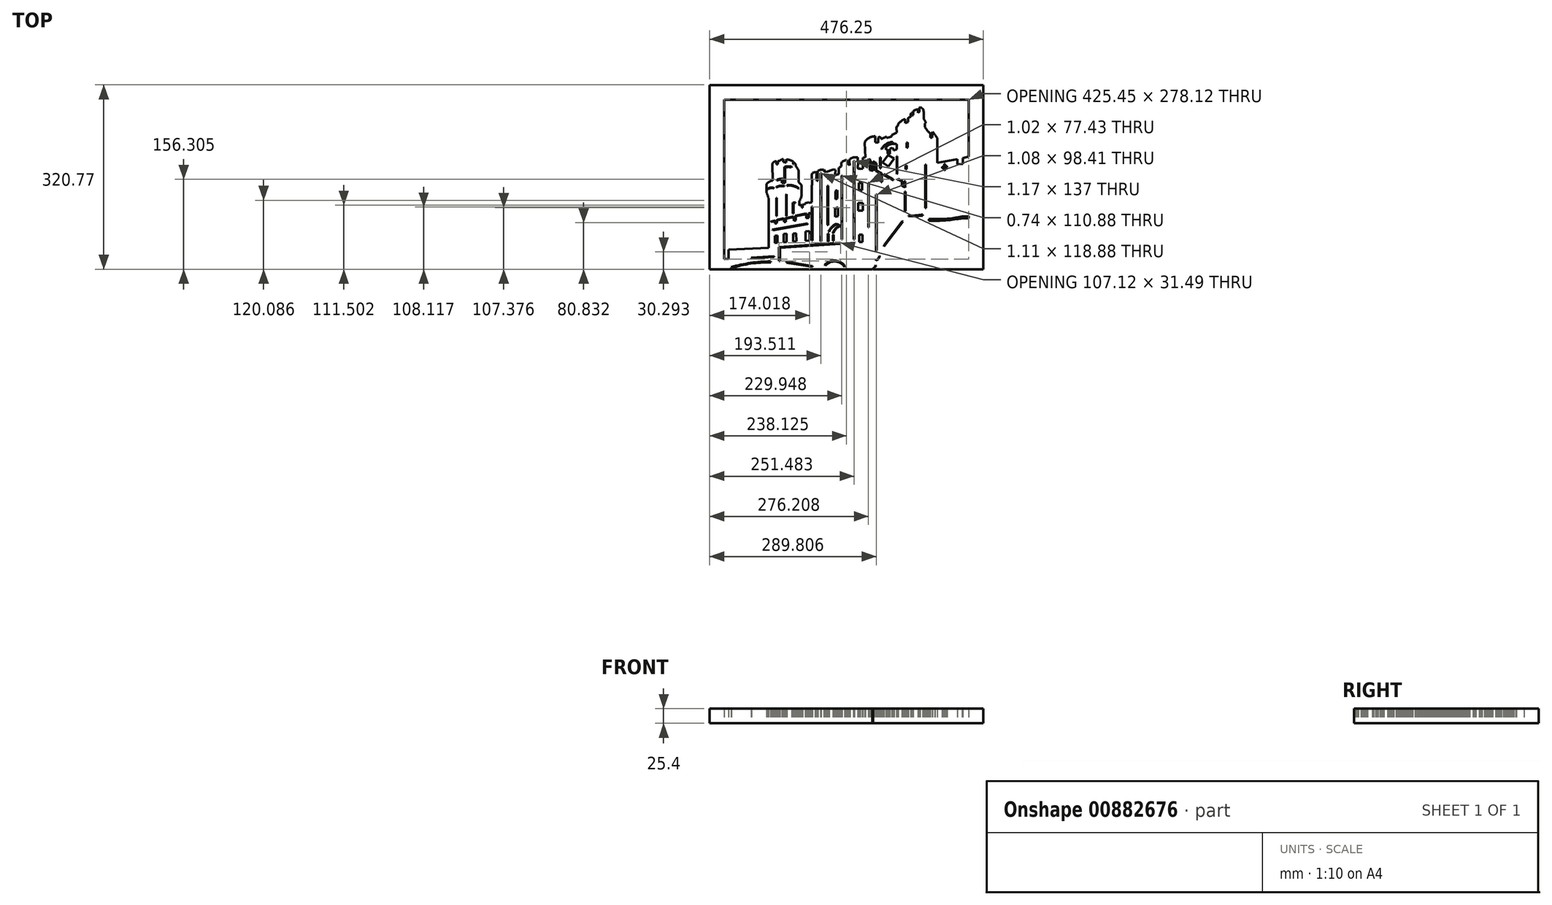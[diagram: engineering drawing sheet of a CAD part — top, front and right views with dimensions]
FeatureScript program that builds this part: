
annotation { "Feature Type Name" : "Feature", "Feature Type Description" : "" }
export const myFeature = defineFeature(function(context is Context, id is Id, definition is map)
    precondition{}
    {
        {
            var Q0;
            Q0=qCreatedBy(makeId("Top.planeOp"),FACE);
            var sketch = newSketch(context, id + "F0", { "sketchPlane" : qUnion([Q0])});
            skLineSegment(sketch, "E0", {"start": v(-417.82, 33.8) * mm, "end": v(-348.2, 37.39) * mm});
            skLineSegment(sketch, "E1", {"start": v(-348.2, 37.39) * mm, "end": v(-348.2, 120.56) * mm});
            skLineSegment(sketch, "E2", {"start": v(-348.2, 120.56) * mm, "end": v(-348.2, 123.62) * mm});
            skLineSegment(sketch, "E3", {"start": v(-348.2, 123.62) * mm, "end": v(-349.5, 125.19) * mm});
            skLineSegment(sketch, "E4", {"start": v(-349.5, 125.19) * mm, "end": v(-349.5, 127.92) * mm});
            skLineSegment(sketch, "E5", {"start": v(-349.5, 127.92) * mm, "end": v(-350.58, 129.49) * mm});
            skLineSegment(sketch, "E6", {"start": v(-350.58, 129.49) * mm, "end": v(-350.58, 131.44) * mm});
            skLineSegment(sketch, "E7", {"start": v(-350.58, 131.44) * mm, "end": v(-351.85, 133) * mm});
            skLineSegment(sketch, "E8", {"start": v(-351.85, 133) * mm, "end": v(-351.85, 148.63) * mm});
            skArc(sketch, "E9", {"start": v(-338.96, 154.6) * mm, "mid": v(-346, 152.92) * mm, "end": v(-351.85, 148.63) * mm});
            skLineSegment(sketch, "E10", {"start": v(-341.3, 154.37) * mm, "end": v(-342.08, 182.63) * mm});
            skLineSegment(sketch, "E11", {"start": v(-334.85, 187.8) * mm, "end": v(-334.85, 182.73) * mm});
            skLineSegment(sketch, "E12", {"start": v(-332.02, 188.4) * mm, "end": v(-332.02, 182.83) * mm});
            skLineSegment(sketch, "E13", {"start": v(-322.54, 191.42) * mm, "end": v(-322.54, 186.15) * mm});
            skLineSegment(sketch, "E14", {"start": v(-317.95, 191.23) * mm, "end": v(-317.95, 185.85) * mm});
            skLineSegment(sketch, "E15", {"start": v(-305.55, 187.32) * mm, "end": v(-305.55, 182.63) * mm});
            skLineSegment(sketch, "E16", {"start": v(-304.86, 186.15) * mm, "end": v(-304.86, 182.63) * mm});
            skLineSegment(sketch, "E17", {"start": v(-301.15, 182.63) * mm, "end": v(-301.15, 179.4) * mm});
            skLineSegment(sketch, "E18", {"start": v(-301.15, 179.4) * mm, "end": v(-298.12, 175.6) * mm});
            skLineSegment(sketch, "E19", {"start": v(-298.12, 175.6) * mm, "end": v(-298.12, 174.42) * mm});
            skLineSegment(sketch, "E20", {"start": v(-298.12, 174.42) * mm, "end": v(-296.26, 172.76) * mm});
            skLineSegment(sketch, "E21", {"start": v(-296.26, 172.76) * mm, "end": v(-296.26, 151.56) * mm});
            skLineSegment(sketch, "E22", {"start": v(-296.26, 151.56) * mm, "end": v(-295, 150.2) * mm});
            skLineSegment(sketch, "E23", {"start": v(-295, 150.2) * mm, "end": v(-294.62, 150.54) * mm});
            skLineSegment(sketch, "E24", {"start": v(-294.62, 150.54) * mm, "end": v(-291.12, 146.77) * mm});
            skLineSegment(sketch, "E25", {"start": v(-291.12, 146.77) * mm, "end": v(-291.12, 126.56) * mm});
            skLineSegment(sketch, "E26", {"start": v(-291.12, 126.56) * mm, "end": v(-291.97, 126.56) * mm});
            skLineSegment(sketch, "E27", {"start": v(-291.97, 126.56) * mm, "end": v(-291.97, 125) * mm});
            skLineSegment(sketch, "E28", {"start": v(-291.97, 125) * mm, "end": v(-291.97, 123.72) * mm});
            skLineSegment(sketch, "E29", {"start": v(-291.97, 123.72) * mm, "end": v(-293.24, 123.72) * mm});
            skLineSegment(sketch, "E30", {"start": v(-293.24, 123.72) * mm, "end": v(-293.72, 119.86) * mm});
            skLineSegment(sketch, "E31", {"start": v(-293.72, 119.86) * mm, "end": v(-294.7, 119.13) * mm});
            skLineSegment(sketch, "E32", {"start": v(-294.7, 119.13) * mm, "end": v(-294.7, 110.83) * mm});
            skLineSegment(sketch, "E33", {"start": v(-294.7, 110.83) * mm, "end": v(-291.77, 111.56) * mm});
            skLineSegment(sketch, "E34", {"start": v(-291.77, 111.56) * mm, "end": v(-290.52, 111.34) * mm});
            skLineSegment(sketch, "E35", {"start": v(-290.52, 111.34) * mm, "end": v(-290.64, 106.87) * mm});
            skLineSegment(sketch, "E36", {"start": v(-290.64, 106.87) * mm, "end": v(-289.3, 107.1) * mm});
            skLineSegment(sketch, "E37", {"start": v(-289.3, 107.1) * mm, "end": v(-289.42, 112.1) * mm});
            skLineSegment(sketch, "E38", {"start": v(-289.42, 112.1) * mm, "end": v(-284.54, 113.5) * mm});
            skLineSegment(sketch, "E39", {"start": v(-284.54, 113.5) * mm, "end": v(-284.6, 114.66) * mm});
            skLineSegment(sketch, "E40", {"start": v(-284.6, 114.66) * mm, "end": v(-278.44, 116.4) * mm});
            skLineSegment(sketch, "E41", {"start": v(-278.44, 116.4) * mm, "end": v(-278.44, 115.41) * mm});
            skLineSegment(sketch, "E42", {"start": v(-278.44, 115.41) * mm, "end": v(-273.18, 116.66) * mm});
            skLineSegment(sketch, "E43", {"start": v(-273.18, 116.66) * mm, "end": v(-273.18, 145.82) * mm});
            skLineSegment(sketch, "E44", {"start": v(-273.18, 145.82) * mm, "end": v(-272.9, 146.87) * mm});
            skLineSegment(sketch, "E45", {"start": v(-272.9, 146.87) * mm, "end": v(-273.18, 165.14) * mm});
            skLineSegment(sketch, "E46", {"start": v(-273.18, 165.14) * mm, "end": v(-271.8, 167.56) * mm});
            skLineSegment(sketch, "E47", {"start": v(-271.8, 167.56) * mm, "end": v(-267.44, 169.08) * mm});
            skLineSegment(sketch, "E48", {"start": v(-267.44, 169.08) * mm, "end": v(-265.5, 168.53) * mm});
            skLineSegment(sketch, "E49", {"start": v(-265.5, 168.53) * mm, "end": v(-264.81, 166.87) * mm});
            skLineSegment(sketch, "E50", {"start": v(-264.81, 166.87) * mm, "end": v(-264.81, 161.9) * mm});
            skLineSegment(sketch, "E51", {"start": v(-264.81, 161.9) * mm, "end": v(-265.23, 160.93) * mm});
            skLineSegment(sketch, "E52", {"start": v(-265.23, 160.93) * mm, "end": v(-265.37, 158.65) * mm});
            skLineSegment(sketch, "E53", {"start": v(-265.37, 158.65) * mm, "end": v(-264.74, 158.3) * mm});
            skLineSegment(sketch, "E54", {"start": v(-264.74, 158.3) * mm, "end": v(-264.6, 153.2) * mm});
            skLineSegment(sketch, "E55", {"start": v(-264.6, 153.2) * mm, "end": v(-262.88, 153.95) * mm});
            skLineSegment(sketch, "E56", {"start": v(-262.88, 153.95) * mm, "end": v(-263.22, 168.46) * mm});
            skLineSegment(sketch, "E57", {"start": v(-263.22, 168.46) * mm, "end": v(-262.46, 171.15) * mm});
            skLineSegment(sketch, "E58", {"start": v(-262.46, 171.15) * mm, "end": v(-257.77, 173.09) * mm});
            skLineSegment(sketch, "E59", {"start": v(-257.77, 173.09) * mm, "end": v(-252.52, 172.95) * mm});
            skLineSegment(sketch, "E60", {"start": v(-252.52, 172.95) * mm, "end": v(-250.72, 170.25) * mm});
            skLineSegment(sketch, "E61", {"start": v(-250.72, 170.25) * mm, "end": v(-250.93, 169.9) * mm});
            skLineSegment(sketch, "E62", {"start": v(-250.93, 169.9) * mm, "end": v(-251.2, 169.29) * mm});
            skLineSegment(sketch, "E63", {"start": v(-251.2, 169.29) * mm, "end": v(-249.75, 169.84) * mm});
            skLineSegment(sketch, "E64", {"start": v(-249.75, 169.84) * mm, "end": v(-247.82, 169.29) * mm});
            skLineSegment(sketch, "E65", {"start": v(-247.82, 169.29) * mm, "end": v(-235.04, 173.91) * mm});
            skLineSegment(sketch, "E66", {"start": v(-235.04, 173.91) * mm, "end": v(-232.9, 173.22) * mm});
            skLineSegment(sketch, "E67", {"start": v(-232.9, 173.22) * mm, "end": v(-232.2, 171.63) * mm});
            skLineSegment(sketch, "E68", {"start": v(-232.2, 171.63) * mm, "end": v(-232.48, 164.86) * mm});
            skLineSegment(sketch, "E69", {"start": v(-232.48, 164.86) * mm, "end": v(-233.06, 164.41) * mm});
            skLineSegment(sketch, "E70", {"start": v(-233.06, 164.41) * mm, "end": v(-233.06, 163.4) * mm});
            skLineSegment(sketch, "E71", {"start": v(-233.06, 163.4) * mm, "end": v(-226.35, 165.63) * mm});
            skLineSegment(sketch, "E72", {"start": v(-226.35, 165.63) * mm, "end": v(-226.35, 174.75) * mm});
            skLineSegment(sketch, "E73", {"start": v(-226.35, 174.75) * mm, "end": v(-225.83, 176.73) * mm});
            skLineSegment(sketch, "E74", {"start": v(-225.83, 176.73) * mm, "end": v(-221.94, 178.7) * mm});
            skLineSegment(sketch, "E75", {"start": v(-221.94, 178.7) * mm, "end": v(-221.94, 184.4) * mm});
            skLineSegment(sketch, "E76", {"start": v(-221.94, 184.4) * mm, "end": v(-220.25, 187.41) * mm});
            skLineSegment(sketch, "E77", {"start": v(-220.25, 187.41) * mm, "end": v(-213.63, 189.97) * mm});
            skLineSegment(sketch, "E78", {"start": v(-213.63, 189.97) * mm, "end": v(-211.6, 189.1) * mm});
            skLineSegment(sketch, "E79", {"start": v(-211.6, 189.1) * mm, "end": v(-210.75, 187.43) * mm});
            skLineSegment(sketch, "E80", {"start": v(-210.75, 187.43) * mm, "end": v(-210.75, 183.11) * mm});
            skLineSegment(sketch, "E81", {"start": v(-210.75, 183.11) * mm, "end": v(-209.16, 182.36) * mm});
            skLineSegment(sketch, "E82", {"start": v(-209.16, 182.36) * mm, "end": v(-207.47, 180.5) * mm});
            skLineSegment(sketch, "E83", {"start": v(-207.47, 180.5) * mm, "end": v(-207.7, 189.68) * mm});
            skLineSegment(sketch, "E84", {"start": v(-207.7, 189.68) * mm, "end": v(-206.6, 192.23) * mm});
            skLineSegment(sketch, "E85", {"start": v(-206.6, 192.23) * mm, "end": v(-200.85, 194.73) * mm});
            skLineSegment(sketch, "E86", {"start": v(-200.85, 194.73) * mm, "end": v(-193.01, 194.85) * mm});
            skLineSegment(sketch, "E87", {"start": v(-193.01, 194.85) * mm, "end": v(-192.78, 181.55) * mm});
            skLineSegment(sketch, "E88", {"start": v(-192.78, 181.55) * mm, "end": v(-193.53, 180.68) * mm});
            skLineSegment(sketch, "E89", {"start": v(-193.53, 180.68) * mm, "end": v(-193.42, 175.74) * mm});
            skLineSegment(sketch, "E90", {"start": v(-193.42, 175.74) * mm, "end": v(-192.55, 175.04) * mm});
            skLineSegment(sketch, "E91", {"start": v(-192.55, 175.04) * mm, "end": v(-189, 175.1) * mm});
            skLineSegment(sketch, "E92", {"start": v(-189, 175.1) * mm, "end": v(-189.06, 174.52) * mm});
            skLineSegment(sketch, "E93", {"start": v(-189.06, 174.52) * mm, "end": v(-184.3, 174.75) * mm});
            skLineSegment(sketch, "E94", {"start": v(-184.3, 174.75) * mm, "end": v(-184.65, 194.33) * mm});
            skLineSegment(sketch, "E95", {"start": v(-184.65, 194.33) * mm, "end": v(-180.17, 194.44) * mm});
            skLineSegment(sketch, "E96", {"start": v(-180.17, 194.44) * mm, "end": v(-180.99, 220.35) * mm});
            skLineSegment(sketch, "E97", {"start": v(-180.99, 220.35) * mm, "end": v(-180.35, 220.99) * mm});
            skLineSegment(sketch, "E98", {"start": v(-180.35, 220.99) * mm, "end": v(-180.35, 222.67) * mm});
            skLineSegment(sketch, "E99", {"start": v(-162.98, 231.27) * mm, "end": v(-162.69, 220.47) * mm});
            skLineSegment(sketch, "E100", {"start": v(-162.69, 220.47) * mm, "end": v(-157.4, 220.35) * mm});
            skLineSegment(sketch, "E101", {"start": v(-157.4, 220.35) * mm, "end": v(-157.8, 228.66) * mm});
            skLineSegment(sketch, "E102", {"start": v(-157.8, 228.66) * mm, "end": v(-156.59, 230.51) * mm});
            skLineSegment(sketch, "E103", {"start": v(-152.76, 228.37) * mm, "end": v(-152.81, 226.74) * mm});
            skLineSegment(sketch, "E104", {"start": v(-152.81, 226.74) * mm, "end": v(-143.17, 230.75) * mm});
            skLineSegment(sketch, "E105", {"start": v(-143.17, 230.75) * mm, "end": v(-143, 228.2) * mm});
            skLineSegment(sketch, "E106", {"start": v(-143, 228.2) * mm, "end": v(-134.4, 231.15) * mm});
            skLineSegment(sketch, "E107", {"start": v(-134.4, 231.15) * mm, "end": v(-134.4, 233.42) * mm});
            skLineSegment(sketch, "E108", {"start": v(-134.4, 233.42) * mm, "end": v(-125.63, 237.72) * mm});
            skLineSegment(sketch, "E109", {"start": v(-125.63, 237.72) * mm, "end": v(-126.2, 246.37) * mm});
            skLineSegment(sketch, "E110", {"start": v(-126.2, 246.37) * mm, "end": v(-124.52, 249.63) * mm});
            skLineSegment(sketch, "E111", {"start": v(-124.52, 249.63) * mm, "end": v(-123.36, 249.63) * mm});
            skLineSegment(sketch, "E112", {"start": v(-123.36, 249.63) * mm, "end": v(-123.36, 252) * mm});
            skLineSegment(sketch, "E113", {"start": v(-110.99, 261.3) * mm, "end": v(-110.99, 259.68) * mm});
            skLineSegment(sketch, "E114", {"start": v(-110.99, 259.68) * mm, "end": v(-110.58, 259.68) * mm});
            skLineSegment(sketch, "E115", {"start": v(-110.58, 259.68) * mm, "end": v(-110.58, 254.16) * mm});
            skLineSegment(sketch, "E116", {"start": v(-110.58, 254.16) * mm, "end": v(-105.53, 256.07) * mm});
            skLineSegment(sketch, "E117", {"start": v(-105.53, 256.07) * mm, "end": v(-105.53, 263.4) * mm});
            skLineSegment(sketch, "E118", {"start": v(-101.23, 269.96) * mm, "end": v(-101.23, 267.34) * mm});
            skLineSegment(sketch, "E119", {"start": v(-101.23, 267.34) * mm, "end": v(-100.3, 266.12) * mm});
            skLineSegment(sketch, "E120", {"start": v(-100.3, 266.12) * mm, "end": v(-100.3, 265.43) * mm});
            skLineSegment(sketch, "E121", {"start": v(-101.23, 269.96) * mm, "end": v(-99.84, 271.93) * mm});
            skLineSegment(sketch, "E122", {"start": v(-99.84, 271.93) * mm, "end": v(-98.9, 271.93) * mm});
            skLineSegment(sketch, "E123", {"start": v(-98.9, 271.93) * mm, "end": v(-98.15, 270.94) * mm});
            skLineSegment(sketch, "E124", {"start": v(-98.15, 270.94) * mm, "end": v(-98.58, 270.4) * mm});
            skLineSegment(sketch, "E125", {"start": v(-98.58, 270.4) * mm, "end": v(-98.58, 268.34) * mm});
            skLineSegment(sketch, "E126", {"start": v(-98.58, 268.34) * mm, "end": v(-97.95, 267.75) * mm});
            skLineSegment(sketch, "E127", {"start": v(-97.95, 267.75) * mm, "end": v(-96.44, 268.5) * mm});
            skLineSegment(sketch, "E128", {"start": v(-96.44, 268.5) * mm, "end": v(-96.44, 274.96) * mm});
            skLineSegment(sketch, "E129", {"start": v(-88.42, 277.86) * mm, "end": v(-88.42, 272.05) * mm});
            skLineSegment(sketch, "E130", {"start": v(-88.42, 272.05) * mm, "end": v(-86.15, 274.09) * mm});
            skLineSegment(sketch, "E131", {"start": v(-86.15, 274.09) * mm, "end": v(-86.15, 281.17) * mm});
            skLineSegment(sketch, "E132", {"start": v(-86.15, 281.17) * mm, "end": v(-84.83, 282.36) * mm});
            skLineSegment(sketch, "E133", {"start": v(-78.9, 277.8) * mm, "end": v(-78.9, 276.87) * mm});
            skLineSegment(sketch, "E134", {"start": v(-78.9, 276.87) * mm, "end": v(-79.24, 276.61) * mm});
            skLineSegment(sketch, "E135", {"start": v(-79.24, 276.61) * mm, "end": v(-79.24, 274.96) * mm});
            skLineSegment(sketch, "E136", {"start": v(-79.24, 274.96) * mm, "end": v(-78.28, 274.46) * mm});
            skLineSegment(sketch, "E137", {"start": v(-78.28, 274.46) * mm, "end": v(-78.28, 261.63) * mm});
            skLineSegment(sketch, "E138", {"start": v(-75.28, 255.92) * mm, "end": v(-75.28, 254.54) * mm});
            skLineSegment(sketch, "E139", {"start": v(-75.28, 254.54) * mm, "end": v(-76.1, 253.85) * mm});
            skLineSegment(sketch, "E140", {"start": v(-76.1, 253.85) * mm, "end": v(-76.18, 247.29) * mm});
            skLineSegment(sketch, "E141", {"start": v(-76.18, 247.29) * mm, "end": v(-71.83, 241.14) * mm});
            skLineSegment(sketch, "E142", {"start": v(-71.83, 241.14) * mm, "end": v(-71.69, 239.7) * mm});
            skLineSegment(sketch, "E143", {"start": v(-71.69, 239.7) * mm, "end": v(-70.88, 239.77) * mm});
            skLineSegment(sketch, "E144", {"start": v(-70.88, 239.77) * mm, "end": v(-67.2, 235.96) * mm});
            skLineSegment(sketch, "E145", {"start": v(-67.2, 235.96) * mm, "end": v(-67.2, 229.12) * mm});
            skLineSegment(sketch, "E146", {"start": v(-67.2, 229.12) * mm, "end": v(-64.02, 229.12) * mm});
            skLineSegment(sketch, "E147", {"start": v(-64.02, 229.12) * mm, "end": v(-64.02, 237.48) * mm});
            skLineSegment(sketch, "E148", {"start": v(-64.02, 237.48) * mm, "end": v(-63.26, 239.14) * mm});
            skLineSegment(sketch, "E149", {"start": v(-63.26, 239.14) * mm, "end": v(-59.18, 234.5) * mm});
            skLineSegment(sketch, "E150", {"start": v(-59.18, 234.5) * mm, "end": v(-59.18, 233.4) * mm});
            skLineSegment(sketch, "E151", {"start": v(-59.18, 233.4) * mm, "end": v(-58.45, 233.22) * mm});
            skLineSegment(sketch, "E152", {"start": v(-58.45, 233.22) * mm, "end": v(-55, 228.36) * mm});
            skLineSegment(sketch, "E153", {"start": v(-55, 228.36) * mm, "end": v(-55, 185.15) * mm});
            skLineSegment(sketch, "E154", {"start": v(-55, 185.15) * mm, "end": v(-20.1, 191.5) * mm});
            skLineSegment(sketch, "E155", {"start": v(-20.1, 191.5) * mm, "end": v(-20.1, 182.51) * mm});
            skLineSegment(sketch, "E156", {"start": v(-20.1, 182.51) * mm, "end": v(-10.63, 183.4) * mm});
            skLineSegment(sketch, "E157", {"start": v(-10.63, 183.4) * mm, "end": v(-10.63, 193.16) * mm});
            skLineSegment(sketch, "E158", {"start": v(-10.63, 193.16) * mm, "end": v(0, 195.7) * mm});
            skArc(sketch, "E159", {"start": v(-334.85, 187.8) * mm, "mid": v(-339.36, 186.46) * mm, "end": v(-342.08, 182.63) * mm});
            skArc(sketch, "E160", {"start": v(-322.54, 191.42) * mm, "mid": v(-326.28, 190.63) * mm, "end": v(-329.38, 188.4) * mm});
            skArc(sketch, "E161", {"start": v(-305.55, 187.32) * mm, "mid": v(-311.5, 190.08) * mm, "end": v(-317.95, 191.23) * mm});
            skLineSegment(sketch, "E162", {"start": v(-304.86, 186.15) * mm, "end": v(-301.15, 182.63) * mm});
            skLineSegment(sketch, "E163", {"start": v(-329.38, 188.4) * mm, "end": v(-332.02, 188.4) * mm});
            skLineSegment(sketch, "E164", {"start": v(-332.02, 182.83) * mm, "end": v(-334.85, 182.73) * mm});
            skArc(sketch, "E165", {"start": v(-317.95, 185.85) * mm, "mid": v(-320.23, 186.22) * mm, "end": v(-322.54, 186.15) * mm});
            skLineSegment(sketch, "E166", {"start": v(-304.86, 182.63) * mm, "end": v(-305.55, 182.63) * mm});
            skArc(sketch, "E167", {"start": v(-162.98, 231.27) * mm, "mid": v(-172.68, 229.03) * mm, "end": v(-180.35, 222.67) * mm});
            skArc(sketch, "E168", {"start": v(-152.76, 228.37) * mm, "mid": v(-154.48, 229.79) * mm, "end": v(-156.59, 230.51) * mm});
            skArc(sketch, "E169", {"start": v(-110.99, 261.3) * mm, "mid": v(-117.84, 257.54) * mm, "end": v(-123.36, 252) * mm});
            skArc(sketch, "E170", {"start": v(-100.3, 265.43) * mm, "mid": v(-103.02, 264.69) * mm, "end": v(-105.53, 263.4) * mm});
            skArc(sketch, "E171", {"start": v(-88.42, 277.86) * mm, "mid": v(-92.77, 277.35) * mm, "end": v(-96.44, 274.96) * mm});
            skArc(sketch, "E172", {"start": v(-78.9, 277.8) * mm, "mid": v(-81.66, 280.35) * mm, "end": v(-84.83, 282.36) * mm});
            skArc(sketch, "E173", {"start": v(-75.28, 255.92) * mm, "mid": v(-76.56, 258.9) * mm, "end": v(-78.28, 261.63) * mm});
            skLineSegment(sketch, "E174.bottom", {"start": v(0, 0) * mm, "end": v(-425.45, 0) * mm});
            skLineSegment(sketch, "E174.top", {"start": v(0, 295.37) * mm, "end": v(-425.45, 295.37) * mm});
            skLineSegment(sketch, "E174.left", {"start": v(0, 0) * mm, "end": v(0, 295.37) * mm});
            skLineSegment(sketch, "E174.right", {"start": v(-425.45, 17.24) * mm, "end": v(-425.45, 295.37) * mm});
            skLineSegment(sketch, "E175", {"start": v(-417.82, 33.8) * mm, "end": v(-417.82, 18.22) * mm});
            skLineSegment(sketch, "E176", {"start": v(-417.82, 18.22) * mm, "end": v(-425.45, 17.24) * mm});
            skLineSegment(sketch, "E177", {"start": v(-115.55, 83.88) * mm, "end": v(-147.82, 41.94) * mm});
            skLineSegment(sketch, "E178", {"start": v(-147.82, 41.94) * mm, "end": v(-147.82, 39.84) * mm});
            skLineSegment(sketch, "E179", {"start": v(-147.82, 39.84) * mm, "end": v(-114.82, 82.86) * mm});
            skLineSegment(sketch, "E180", {"start": v(-114.82, 82.86) * mm, "end": v(-115.55, 83.88) * mm});
            skArc(sketch, "E181", {"start": v(-69.74, 87.47) * mm, "mid": v(-40.42, 87.66) * mm, "end": v(-11.37, 91.58) * mm});
            skArc(sketch, "E182", {"start": v(-69.74, 84.45) * mm, "mid": v(-40.17, 85.13) * mm, "end": v(-10.82, 88.84) * mm});
            skLineSegment(sketch, "E183", {"start": v(-69.74, 84.45) * mm, "end": v(-69.74, 87.47) * mm});
            skLineSegment(sketch, "E184", {"start": v(-10.82, 88.84) * mm, "end": v(-11.37, 91.58) * mm});
            skLineSegment(sketch, "E185", {"start": v(-108.23, 174.38) * mm, "end": v(-108.23, 180.96) * mm});
            skLineSegment(sketch, "E186", {"start": v(-108.23, 180.96) * mm, "end": v(-110.07, 180.29) * mm});
            skLineSegment(sketch, "E187", {"start": v(-110.07, 180.29) * mm, "end": v(-110.07, 173.7) * mm});
            skLineSegment(sketch, "E188", {"start": v(-110.07, 173.7) * mm, "end": v(-108.23, 174.38) * mm});
            skLineSegment(sketch, "E189", {"start": v(-106.18, 220.87) * mm, "end": v(-108.12, 220.2) * mm});
            skLineSegment(sketch, "E190", {"start": v(-108.12, 220.2) * mm, "end": v(-108.02, 210.99) * mm});
            skLineSegment(sketch, "E191", {"start": v(-108.02, 210.99) * mm, "end": v(-106.18, 211.86) * mm});
            skLineSegment(sketch, "E192", {"start": v(-106.18, 211.86) * mm, "end": v(-106.18, 220.87) * mm});
            skLineSegment(sketch, "E193", {"start": v(-144.26, 211.67) * mm, "end": v(-144.26, 208.08) * mm});
            skLineSegment(sketch, "E194", {"start": v(-144.26, 208.08) * mm, "end": v(-140.97, 208.86) * mm});
            skLineSegment(sketch, "E195", {"start": v(-140.97, 208.86) * mm, "end": v(-140.97, 201.1) * mm});
            skLineSegment(sketch, "E196", {"start": v(-140.97, 201.1) * mm, "end": v(-139.7, 201.1) * mm});
            skLineSegment(sketch, "E197", {"start": v(-139.7, 201.1) * mm, "end": v(-139.7, 200.28) * mm});
            skLineSegment(sketch, "E198", {"start": v(-139.7, 200.28) * mm, "end": v(-137.1, 200.62) * mm});
            skLineSegment(sketch, "E199", {"start": v(-137.1, 200.62) * mm, "end": v(-137.1, 209.6) * mm});
            skLineSegment(sketch, "E200", {"start": v(-137.1, 209.6) * mm, "end": v(-133.78, 211.51) * mm});
            skLineSegment(sketch, "E201", {"start": v(-133.78, 211.51) * mm, "end": v(-130.79, 209.1) * mm});
            skLineSegment(sketch, "E202", {"start": v(-130.79, 209.1) * mm, "end": v(-130.79, 206.84) * mm});
            skLineSegment(sketch, "E203", {"start": v(-130.79, 206.84) * mm, "end": v(-125.34, 208.8) * mm});
            skLineSegment(sketch, "E204", {"start": v(-125.34, 208.8) * mm, "end": v(-125.34, 217.39) * mm});
            skArc(sketch, "E205", {"start": v(-125.34, 217.39) * mm, "mid": v(-135.76, 217.7) * mm, "end": v(-144.26, 211.67) * mm});
            skLineSegment(sketch, "E206", {"start": v(-42.6, 183.06) * mm, "end": v(-42.6, 178.05) * mm});
            skArc(sketch, "E207", {"start": v(-45.61, 178.23) * mm, "mid": v(-46.35, 177) * mm, "end": v(-45.44, 175.9) * mm});
            skArc(sketch, "E208", {"start": v(-38.3, 177.28) * mm, "mid": v(-37.9, 178.49) * mm, "end": v(-38.73, 179.44) * mm});
            skArc(sketch, "E209", {"start": v(-43.14, 174.09) * mm, "mid": v(-41.82, 172.7) * mm, "end": v(-40.48, 174.06) * mm});
            skArc(sketch, "E210", {"start": v(-43.14, 174.09) * mm, "mid": v(-42.7, 174.67) * mm, "end": v(-42.46, 175.37) * mm});
            skArc(sketch, "E211", {"start": v(-41.25, 175.32) * mm, "mid": v(-40.92, 174.66) * mm, "end": v(-40.48, 174.06) * mm});
            skArc(sketch, "E212", {"start": v(-38.73, 179.44) * mm, "mid": v(-39.25, 179.03) * mm, "end": v(-39.75, 178.62) * mm});
            skArc(sketch, "E213", {"start": v(-44.55, 177.6) * mm, "mid": v(-45.04, 177.98) * mm, "end": v(-45.61, 178.23) * mm});
            skArc(sketch, "E214", {"start": v(-45.44, 175.9) * mm, "mid": v(-44.93, 176.13) * mm, "end": v(-44.6, 176.58) * mm});
            skLineSegment(sketch, "E215", {"start": v(-42.6, 183.06) * mm, "end": v(-41.67, 183.06) * mm});
            skLineSegment(sketch, "E216", {"start": v(-41.67, 183.06) * mm, "end": v(-41.67, 178.47) * mm});
            skLineSegment(sketch, "E217", {"start": v(-41.67, 178.47) * mm, "end": v(-39.75, 178.62) * mm});
            skLineSegment(sketch, "E218", {"start": v(-38.3, 177.28) * mm, "end": v(-40.99, 177.28) * mm});
            skLineSegment(sketch, "E219", {"start": v(-40.99, 177.28) * mm, "end": v(-41.52, 176.78) * mm});
            skLineSegment(sketch, "E220", {"start": v(-41.52, 176.78) * mm, "end": v(-41.19, 175.17) * mm});
            skLineSegment(sketch, "E221", {"start": v(-42.46, 175.37) * mm, "end": v(-42.46, 176.85) * mm});
            skLineSegment(sketch, "E222", {"start": v(-42.46, 176.85) * mm, "end": v(-44.35, 176.85) * mm});
            skLineSegment(sketch, "E223", {"start": v(-44.35, 176.85) * mm, "end": v(-44.6, 176.58) * mm});
            skLineSegment(sketch, "E224", {"start": v(-44.55, 177.6) * mm, "end": v(-43.58, 177.6) * mm});
            skLineSegment(sketch, "E225", {"start": v(-43.58, 177.6) * mm, "end": v(-43.29, 178.05) * mm});
            skLineSegment(sketch, "E226", {"start": v(-43.29, 178.05) * mm, "end": v(-42.6, 178.05) * mm});
            skArc(sketch, "E227", {"start": v(-105.02, 92.23) * mm, "mid": v(-92.7, 92.4) * mm, "end": v(-80.4, 93.39) * mm});
            skArc(sketch, "E228", {"start": v(-105.02, 93.31) * mm, "mid": v(-92.66, 93.49) * mm, "end": v(-80.4, 95.06) * mm});
            skLineSegment(sketch, "E229", {"start": v(-105.02, 93.31) * mm, "end": v(-105.02, 92.23) * mm});
            skLineSegment(sketch, "E230", {"start": v(-80.4, 95.06) * mm, "end": v(-80.4, 93.39) * mm});
            skLineSegment(sketch, "E231", {"start": v(-223.27, 44.53) * mm, "end": v(-328.37, 37.04) * mm});
            skLineSegment(sketch, "E232", {"start": v(-328.37, 37.04) * mm, "end": v(-328.37, 14.55) * mm});
            skLineSegment(sketch, "E233", {"start": v(-328.37, 14.55) * mm, "end": v(-330.4, 14.55) * mm});
            skLineSegment(sketch, "E234", {"start": v(-330.4, 14.55) * mm, "end": v(-330.4, 38.29) * mm});
            skLineSegment(sketch, "E235", {"start": v(-330.4, 38.29) * mm, "end": v(-223.52, 46.04) * mm});
            skLineSegment(sketch, "E236", {"start": v(-223.52, 46.04) * mm, "end": v(-223.27, 44.53) * mm});
            skLineSegment(sketch, "E237", {"start": v(-245.1, 48.1) * mm, "end": v(-245.1, 62.05) * mm});
            skLineSegment(sketch, "E238", {"start": v(-236.2, 49.45) * mm, "end": v(-236.2, 59.53) * mm});
            skLineSegment(sketch, "E239", {"start": v(-221.27, 51.97) * mm, "end": v(-221.27, 162.81) * mm});
            skLineSegment(sketch, "E240", {"start": v(-257.9, 48.68) * mm, "end": v(-257.9, 167.27) * mm});
            skLineSegment(sketch, "E241", {"start": v(-273, 108.75) * mm, "end": v(-273, 50.03) * mm});
            skLineSegment(sketch, "E242", {"start": v(-199.95, 51.58) * mm, "end": v(-199.95, 188.59) * mm});
            skLineSegment(sketch, "E243", {"start": v(-175.15, 150.22) * mm, "end": v(-175.15, 73.1) * mm});
            skLineSegment(sketch, "E244", {"start": v(-161.59, 129.68) * mm, "end": v(-161.59, 31.63) * mm});
            skLineSegment(sketch, "E245", {"start": v(-111.2, 101) * mm, "end": v(-111.2, 134.9) * mm});
            skLineSegment(sketch, "E246", {"start": v(-75.55, 182) * mm, "end": v(-75.55, 106.23) * mm});
            skLineSegment(sketch, "E247", {"start": v(-125.52, 196.51) * mm, "end": v(-125.52, 165.55) * mm});
            skLineSegment(sketch, "E248", {"start": v(-154.3, 194.46) * mm, "end": v(-154.3, 175.55) * mm});
            skLineSegment(sketch, "E249", {"start": v(-245.69, 145.4) * mm, "end": v(-245.69, 77.03) * mm});
            skLineSegment(sketch, "E250", {"start": v(-273, 108.75) * mm, "end": v(-272.1, 108.75) * mm});
            skLineSegment(sketch, "E251", {"start": v(-272.1, 108.75) * mm, "end": v(-272.1, 50.18) * mm});
            skLineSegment(sketch, "E252", {"start": v(-272.1, 50.18) * mm, "end": v(-273, 50.03) * mm});
            skLineSegment(sketch, "E253", {"start": v(-257.9, 48.68) * mm, "end": v(-256.78, 48.68) * mm});
            skLineSegment(sketch, "E254", {"start": v(-256.78, 48.68) * mm, "end": v(-256.78, 167.56) * mm});
            skLineSegment(sketch, "E255", {"start": v(-256.78, 167.56) * mm, "end": v(-257.9, 167.27) * mm});
            skLineSegment(sketch, "E256", {"start": v(-245.69, 145.4) * mm, "end": v(-244.96, 145.4) * mm});
            skLineSegment(sketch, "E257", {"start": v(-244.96, 145.4) * mm, "end": v(-244.96, 76.93) * mm});
            skLineSegment(sketch, "E258", {"start": v(-244.96, 76.93) * mm, "end": v(-245.69, 77.03) * mm});
            skLineSegment(sketch, "E259", {"start": v(-221.27, 162.81) * mm, "end": v(-220.53, 162.81) * mm});
            skLineSegment(sketch, "E260", {"start": v(-220.53, 162.81) * mm, "end": v(-220.53, 51.94) * mm});
            skLineSegment(sketch, "E261", {"start": v(-220.53, 51.94) * mm, "end": v(-221.27, 51.97) * mm});
            skLineSegment(sketch, "E262", {"start": v(-199.95, 51.58) * mm, "end": v(-198.78, 51.58) * mm});
            skLineSegment(sketch, "E263", {"start": v(-198.78, 51.58) * mm, "end": v(-198.78, 188.59) * mm});
            skLineSegment(sketch, "E264", {"start": v(-198.78, 188.59) * mm, "end": v(-199.95, 188.59) * mm});
            skLineSegment(sketch, "E265", {"start": v(-175.15, 150.22) * mm, "end": v(-174.13, 150.22) * mm});
            skLineSegment(sketch, "E266", {"start": v(-174.13, 150.22) * mm, "end": v(-174.13, 72.79) * mm});
            skLineSegment(sketch, "E267", {"start": v(-174.13, 72.79) * mm, "end": v(-175.15, 73.1) * mm});
            skLineSegment(sketch, "E268", {"start": v(-161.59, 129.68) * mm, "end": v(-160.5, 130.04) * mm});
            skLineSegment(sketch, "E269", {"start": v(-160.5, 130.04) * mm, "end": v(-160.5, 32.64) * mm});
            skLineSegment(sketch, "E270", {"start": v(-160.5, 32.64) * mm, "end": v(-161.59, 31.63) * mm});
            skLineSegment(sketch, "E271", {"start": v(-111.2, 101) * mm, "end": v(-109.86, 101.44) * mm});
            skLineSegment(sketch, "E272", {"start": v(-109.86, 101.44) * mm, "end": v(-109.86, 134.9) * mm});
            skLineSegment(sketch, "E273", {"start": v(-109.86, 134.9) * mm, "end": v(-111.2, 134.9) * mm});
            skLineSegment(sketch, "E274", {"start": v(-75.55, 106.23) * mm, "end": v(-74.3, 106.27) * mm});
            skLineSegment(sketch, "E275", {"start": v(-74.3, 106.27) * mm, "end": v(-74.3, 182.18) * mm});
            skLineSegment(sketch, "E276", {"start": v(-74.3, 182.18) * mm, "end": v(-75.55, 182) * mm});
            skLineSegment(sketch, "E277", {"start": v(-125.52, 196.51) * mm, "end": v(-124.65, 196.8) * mm});
            skLineSegment(sketch, "E278", {"start": v(-124.65, 196.8) * mm, "end": v(-124.65, 165.83) * mm});
            skLineSegment(sketch, "E279", {"start": v(-124.65, 165.83) * mm, "end": v(-125.52, 165.55) * mm});
            skLineSegment(sketch, "E280", {"start": v(-154.3, 194.46) * mm, "end": v(-153.5, 194.72) * mm});
            skLineSegment(sketch, "E281", {"start": v(-153.5, 194.72) * mm, "end": v(-153.5, 175.55) * mm});
            skLineSegment(sketch, "E282", {"start": v(-153.5, 175.55) * mm, "end": v(-154.3, 175.55) * mm});
            skLineSegment(sketch, "E283", {"start": v(-245.1, 62.05) * mm, "end": v(-244.28, 62.07) * mm});
            skLineSegment(sketch, "E284", {"start": v(-244.28, 62.07) * mm, "end": v(-244.28, 47.93) * mm});
            skLineSegment(sketch, "E285", {"start": v(-244.28, 47.93) * mm, "end": v(-245.1, 48.1) * mm});
            skLineSegment(sketch, "E286", {"start": v(-236.2, 59.53) * mm, "end": v(-235.4, 59.8) * mm});
            skLineSegment(sketch, "E287", {"start": v(-235.4, 59.8) * mm, "end": v(-235.4, 49.19) * mm});
            skLineSegment(sketch, "E288", {"start": v(-235.4, 49.19) * mm, "end": v(-236.2, 49.45) * mm});
            skArc(sketch, "E289", {"start": v(-230.75, 77.8) * mm, "mid": v(-237.9, 72.6) * mm, "end": v(-242.95, 65.32) * mm});
            skArc(sketch, "E290", {"start": v(-222.34, 73.62) * mm, "mid": v(-226.32, 76.16) * mm, "end": v(-230.75, 77.8) * mm});
            skArc(sketch, "E291.0", {"start": v(-230.86, 78.87) * mm, "mid": v(-238.5, 73.44) * mm, "end": v(-243.87, 65.75) * mm});
            skArc(sketch, "E291.1", {"start": v(-222.34, 74.9) * mm, "mid": v(-226.4, 77.32) * mm, "end": v(-230.86, 78.87) * mm});
            skLineSegment(sketch, "E292", {"start": v(-242.95, 65.32) * mm, "end": v(-243.87, 65.75) * mm});
            skLineSegment(sketch, "E293", {"start": v(-222.34, 73.62) * mm, "end": v(-222.34, 74.9) * mm});
            skArc(sketch, "E294", {"start": v(-226.4, 74.08) * mm, "mid": v(-232.03, 69.2) * mm, "end": v(-235.78, 62.74) * mm});
            skArc(sketch, "E295.0", {"start": v(-226.93, 74.95) * mm, "mid": v(-232.81, 69.84) * mm, "end": v(-236.73, 63.1) * mm});
            skLineSegment(sketch, "E296", {"start": v(-235.78, 62.74) * mm, "end": v(-236.73, 63.1) * mm});
            skLineSegment(sketch, "E297", {"start": v(-226.4, 74.08) * mm, "end": v(-226.93, 74.95) * mm});
            skLineSegment(sketch, "E298", {"start": v(-344.36, 82.85) * mm, "end": v(-336.7, 84.79) * mm});
            skLineSegment(sketch, "E299", {"start": v(-336.7, 84.79) * mm, "end": v(-336.4, 80.75) * mm});
            skLineSegment(sketch, "E300", {"start": v(-336.4, 80.75) * mm, "end": v(-334.96, 80.82) * mm});
            skLineSegment(sketch, "E301", {"start": v(-334.96, 80.82) * mm, "end": v(-334.67, 84.5) * mm});
            skLineSegment(sketch, "E302", {"start": v(-334.67, 84.5) * mm, "end": v(-332.92, 86.24) * mm});
            skLineSegment(sketch, "E303", {"start": v(-332.92, 86.24) * mm, "end": v(-322.07, 88.37) * mm});
            skLineSegment(sketch, "E304", {"start": v(-322.07, 88.37) * mm, "end": v(-320.9, 87.21) * mm});
            skLineSegment(sketch, "E305", {"start": v(-320.9, 87.21) * mm, "end": v(-320.81, 82.95) * mm});
            skLineSegment(sketch, "E306", {"start": v(-320.81, 82.95) * mm, "end": v(-318.97, 83.05) * mm});
            skLineSegment(sketch, "E307", {"start": v(-318.97, 83.05) * mm, "end": v(-318.97, 88.76) * mm});
            skLineSegment(sketch, "E308", {"start": v(-318.97, 88.76) * mm, "end": v(-305.02, 91.86) * mm});
            skLineSegment(sketch, "E309", {"start": v(-305.02, 91.86) * mm, "end": v(-304.15, 90.6) * mm});
            skLineSegment(sketch, "E310", {"start": v(-304.15, 90.6) * mm, "end": v(-303.95, 84.98) * mm});
            skLineSegment(sketch, "E311", {"start": v(-303.95, 84.98) * mm, "end": v(-301.92, 85.08) * mm});
            skLineSegment(sketch, "E312", {"start": v(-301.92, 85.08) * mm, "end": v(-301.82, 93.02) * mm});
            skLineSegment(sketch, "E313", {"start": v(-301.82, 93.02) * mm, "end": v(-283.22, 97) * mm});
            skLineSegment(sketch, "E314", {"start": v(-283.22, 97) * mm, "end": v(-282.25, 96.22) * mm});
            skLineSegment(sketch, "E315", {"start": v(-282.25, 96.22) * mm, "end": v(-282.25, 89.44) * mm});
            skLineSegment(sketch, "E316", {"start": v(-282.25, 89.44) * mm, "end": v(-279.15, 89.73) * mm});
            skLineSegment(sketch, "E317", {"start": v(-279.15, 89.73) * mm, "end": v(-279.15, 97) * mm});
            skLineSegment(sketch, "E318", {"start": v(-279.15, 97) * mm, "end": v(-275.57, 97.97) * mm});
            skLineSegment(sketch, "E319", {"start": v(-275.57, 97.97) * mm, "end": v(-275.52, 97.14) * mm});
            skLineSegment(sketch, "E320", {"start": v(-275.52, 97.14) * mm, "end": v(-278.33, 96.27) * mm});
            skLineSegment(sketch, "E321", {"start": v(-278.33, 96.27) * mm, "end": v(-278.33, 89.34) * mm});
            skLineSegment(sketch, "E322", {"start": v(-278.33, 89.34) * mm, "end": v(-282.83, 88.9) * mm});
            skLineSegment(sketch, "E323", {"start": v(-282.83, 88.9) * mm, "end": v(-283.03, 95.79) * mm});
            skLineSegment(sketch, "E324", {"start": v(-283.03, 95.79) * mm, "end": v(-301.1, 92.2) * mm});
            skLineSegment(sketch, "E325", {"start": v(-301.1, 92.2) * mm, "end": v(-301.2, 84.64) * mm});
            skLineSegment(sketch, "E326", {"start": v(-301.2, 84.64) * mm, "end": v(-304.7, 84.4) * mm});
            skLineSegment(sketch, "E327", {"start": v(-304.7, 84.4) * mm, "end": v(-305.12, 90.25) * mm});
            skLineSegment(sketch, "E328", {"start": v(-305.12, 90.25) * mm, "end": v(-305.65, 90.7) * mm});
            skLineSegment(sketch, "E329", {"start": v(-305.65, 90.7) * mm, "end": v(-318.2, 88.28) * mm});
            skLineSegment(sketch, "E330", {"start": v(-318.2, 88.28) * mm, "end": v(-318.2, 82.32) * mm});
            skLineSegment(sketch, "E331", {"start": v(-318.2, 82.32) * mm, "end": v(-321.43, 82.47) * mm});
            skLineSegment(sketch, "E332", {"start": v(-321.43, 82.47) * mm, "end": v(-321.43, 86.73) * mm});
            skLineSegment(sketch, "E333", {"start": v(-321.43, 86.73) * mm, "end": v(-322.12, 87.5) * mm});
            skLineSegment(sketch, "E334", {"start": v(-322.12, 87.5) * mm, "end": v(-332.54, 85.61) * mm});
            skLineSegment(sketch, "E335", {"start": v(-332.54, 85.61) * mm, "end": v(-333.84, 84.2) * mm});
            skLineSegment(sketch, "E336", {"start": v(-333.84, 84.2) * mm, "end": v(-334.38, 80) * mm});
            skLineSegment(sketch, "E337", {"start": v(-334.38, 80) * mm, "end": v(-337.14, 79.9) * mm});
            skLineSegment(sketch, "E338", {"start": v(-337.14, 79.9) * mm, "end": v(-337.42, 83.77) * mm});
            skLineSegment(sketch, "E339", {"start": v(-337.42, 83.77) * mm, "end": v(-344.3, 82.12) * mm});
            skLineSegment(sketch, "E340", {"start": v(-344.3, 82.12) * mm, "end": v(-344.36, 82.85) * mm});
            skLineSegment(sketch, "E341", {"start": v(-131.32, 156.31) * mm, "end": v(-147.63, 165.22) * mm});
            skLineSegment(sketch, "E342", {"start": v(-147.63, 165.22) * mm, "end": v(-147.26, 163.66) * mm});
            skLineSegment(sketch, "E343", {"start": v(-147.26, 163.66) * mm, "end": v(-130.9, 154.67) * mm});
            skLineSegment(sketch, "E344", {"start": v(-130.9, 154.67) * mm, "end": v(-131.32, 156.31) * mm});
            skArc(sketch, "E345", {"start": v(-308.34, 178.4) * mm, "mid": v(-314.65, 179.04) * mm, "end": v(-320.93, 178.11) * mm});
            skLineSegment(sketch, "E346", {"start": v(-320.93, 178.11) * mm, "end": v(-320.93, 151.37) * mm});
            skLineSegment(sketch, "E347", {"start": v(-320.93, 151.37) * mm, "end": v(-324.32, 151.37) * mm});
            skLineSegment(sketch, "E348", {"start": v(-324.32, 151.37) * mm, "end": v(-324.32, 157.67) * mm});
            skArc(sketch, "E349", {"start": v(-324.32, 157.67) * mm, "mid": v(-329.42, 157.06) * mm, "end": v(-334.4, 155.83) * mm});
            skArc(sketch, "E350", {"start": v(-325.48, 156.12) * mm, "mid": v(-329.9, 155.64) * mm, "end": v(-334.2, 154.47) * mm});
            skArc(sketch, "E351", {"start": v(-308.34, 177.24) * mm, "mid": v(-314.05, 177.91) * mm, "end": v(-319.77, 177.24) * mm});
            skLineSegment(sketch, "E352", {"start": v(-308.34, 178.4) * mm, "end": v(-308.34, 177.24) * mm});
            skLineSegment(sketch, "E353", {"start": v(-319.77, 177.24) * mm, "end": v(-319.77, 150.2) * mm});
            skLineSegment(sketch, "E354", {"start": v(-319.77, 150.2) * mm, "end": v(-325.58, 150.2) * mm});
            skLineSegment(sketch, "E355", {"start": v(-325.58, 150.2) * mm, "end": v(-325.48, 156.12) * mm});
            skLineSegment(sketch, "E356", {"start": v(-334.2, 154.47) * mm, "end": v(-334.4, 155.83) * mm});
            skLineSegment(sketch, "E357", {"start": v(-335.09, 124.08) * mm, "end": v(-335.09, 92.29) * mm});
            skLineSegment(sketch, "E358", {"start": v(-335.09, 92.29) * mm, "end": v(-334.13, 92.29) * mm});
            skLineSegment(sketch, "E359", {"start": v(-334.13, 92.29) * mm, "end": v(-334.13, 124.35) * mm});
            skLineSegment(sketch, "E360", {"start": v(-334.13, 124.35) * mm, "end": v(-335.09, 124.08) * mm});
            skLineSegment(sketch, "E361", {"start": v(-317.55, 130.04) * mm, "end": v(-317.55, 92.5) * mm});
            skLineSegment(sketch, "E362", {"start": v(-317.55, 92.5) * mm, "end": v(-316.8, 92.7) * mm});
            skLineSegment(sketch, "E363", {"start": v(-316.8, 92.7) * mm, "end": v(-316.8, 130.31) * mm});
            skLineSegment(sketch, "E364", {"start": v(-316.8, 130.31) * mm, "end": v(-317.55, 130.04) * mm});
            skLineSegment(sketch, "E365", {"start": v(-280.54, 80) * mm, "end": v(-341.73, 68.9) * mm});
            skLineSegment(sketch, "E366", {"start": v(-341.73, 68.9) * mm, "end": v(-341.5, 67.67) * mm});
            skLineSegment(sketch, "E367", {"start": v(-341.5, 67.67) * mm, "end": v(-280.7, 78.7) * mm});
            skLineSegment(sketch, "E368", {"start": v(-280.7, 78.7) * mm, "end": v(-280.54, 80) * mm});
            skLineSegment(sketch, "E369", {"start": v(-305.04, 96.72) * mm, "end": v(-305.04, 115.35) * mm});
            skLineSegment(sketch, "E370", {"start": v(-305.04, 115.35) * mm, "end": v(-301.56, 115.6) * mm});
            skLineSegment(sketch, "E371.0", {"start": v(-306.06, 116.3) * mm, "end": v(-301.63, 116.61) * mm});
            skLineSegment(sketch, "E371.1", {"start": v(-306.06, 96.72) * mm, "end": v(-306.06, 116.3) * mm});
            skLineSegment(sketch, "E372", {"start": v(-306.06, 96.72) * mm, "end": v(-305.04, 96.72) * mm});
            skLineSegment(sketch, "E373", {"start": v(-301.56, 115.6) * mm, "end": v(-301.63, 116.61) * mm});
            skArc(sketch, "E374", {"start": v(-339.26, 140.78) * mm, "mid": v(-344.65, 141.27) * mm, "end": v(-349.63, 139.17) * mm});
            skArc(sketch, "E375", {"start": v(-320.71, 144.35) * mm, "mid": v(-327.94, 144.52) * mm, "end": v(-334.88, 142.5) * mm});
            skArc(sketch, "E376", {"start": v(-295.94, 140.09) * mm, "mid": v(-305.59, 144.84) * mm, "end": v(-316.33, 145.27) * mm});
            skArc(sketch, "E377", {"start": v(-339.32, 141.64) * mm, "mid": v(-344.7, 141.95) * mm, "end": v(-349.8, 140.26) * mm});
            skArc(sketch, "E378", {"start": v(-320.65, 145.22) * mm, "mid": v(-328.01, 145.17) * mm, "end": v(-335.11, 143.26) * mm});
            skArc(sketch, "E379", {"start": v(-295.65, 140.72) * mm, "mid": v(-305.48, 145.62) * mm, "end": v(-316.45, 146.08) * mm});
            skLineSegment(sketch, "E380", {"start": v(-295.94, 140.09) * mm, "end": v(-295.65, 140.72) * mm});
            skLineSegment(sketch, "E381", {"start": v(-316.33, 145.27) * mm, "end": v(-316.45, 146.08) * mm});
            skLineSegment(sketch, "E382", {"start": v(-320.71, 144.35) * mm, "end": v(-320.65, 145.22) * mm});
            skLineSegment(sketch, "E383", {"start": v(-334.88, 142.5) * mm, "end": v(-335.11, 143.26) * mm});
            skLineSegment(sketch, "E384", {"start": v(-339.26, 140.78) * mm, "end": v(-339.32, 141.64) * mm});
            skLineSegment(sketch, "E385", {"start": v(-349.63, 139.17) * mm, "end": v(-349.8, 140.26) * mm});
            skArc(sketch, "E386", {"start": v(-216.32, 3.83) * mm, "mid": v(-232.39, 13.69) * mm, "end": v(-249.61, 6.02) * mm});
            skArc(sketch, "E387", {"start": v(-215.36, 5.2) * mm, "mid": v(-232.47, 14.94) * mm, "end": v(-250.7, 7.53) * mm});
            skLineSegment(sketch, "E388", {"start": v(-216.32, 3.83) * mm, "end": v(-215.36, 5.2) * mm});
            skLineSegment(sketch, "E389", {"start": v(-249.61, 6.02) * mm, "end": v(-250.7, 7.53) * mm});
            skArc(sketch, "E390", {"start": v(-344.81, 13.6) * mm, "mid": v(-379.62, 10.96) * mm, "end": v(-413.74, 3.6) * mm});
            skArc(sketch, "E391", {"start": v(-344.54, 11.68) * mm, "mid": v(-379.15, 9.7) * mm, "end": v(-412.91, 1.82) * mm});
            skLineSegment(sketch, "E392", {"start": v(-412.91, 1.82) * mm, "end": v(-413.74, 3.6) * mm});
            skLineSegment(sketch, "E393", {"start": v(-344.54, 11.68) * mm, "end": v(-344.81, 13.6) * mm});
            skLineSegment(sketch, "E394", {"start": v(-378.38, 20.18) * mm, "end": v(-338.65, 22.78) * mm});
            skLineSegment(sketch, "E395", {"start": v(-338.65, 22.78) * mm, "end": v(-338.57, 21.54) * mm});
            skLineSegment(sketch, "E396", {"start": v(-338.57, 21.54) * mm, "end": v(-378.25, 18.8) * mm});
            skLineSegment(sketch, "E397", {"start": v(-378.25, 18.8) * mm, "end": v(-378.38, 20.18) * mm});
            skLineSegment(sketch, "E398", {"start": v(-129.53, 192.7) * mm, "end": v(-140.13, 178.54) * mm});
            skLineSegment(sketch, "E399", {"start": v(-140.13, 178.54) * mm, "end": v(-150.1, 185.99) * mm});
            skLineSegment(sketch, "E400", {"start": v(-150.1, 185.99) * mm, "end": v(-140.77, 198.46) * mm});
            skLineSegment(sketch, "E401", {"start": v(-140.77, 198.46) * mm, "end": v(-129.53, 192.7) * mm});
            skArc(sketch, "E402", {"start": v(-132.24, 220.75) * mm, "mid": v(-143.34, 217.22) * mm, "end": v(-151.56, 208.97) * mm});
            skArc(sketch, "E403", {"start": v(-132.52, 221.64) * mm, "mid": v(-143.66, 217.8) * mm, "end": v(-152.11, 209.59) * mm});
            skLineSegment(sketch, "E404", {"start": v(-151.56, 208.97) * mm, "end": v(-152.11, 209.59) * mm});
            skLineSegment(sketch, "E405", {"start": v(-132.24, 220.75) * mm, "end": v(-132.52, 221.64) * mm});
            skLineSegment(sketch, "E406.bottom", {"start": v(-191.51, 150.22) * mm, "end": v(-185.81, 150.22) * mm});
            skLineSegment(sketch, "E406.top", {"start": v(-191.51, 137.35) * mm, "end": v(-185.81, 137.35) * mm});
            skLineSegment(sketch, "E406.left", {"start": v(-191.51, 150.22) * mm, "end": v(-191.51, 137.35) * mm});
            skLineSegment(sketch, "E406.right", {"start": v(-185.81, 150.22) * mm, "end": v(-185.81, 137.35) * mm});
            skLineSegment(sketch, "E407.bottom", {"start": v(-192.33, 115.51) * mm, "end": v(-184.02, 115.51) * mm});
            skLineSegment(sketch, "E407.top", {"start": v(-192.33, 102.15) * mm, "end": v(-184.02, 102.15) * mm});
            skLineSegment(sketch, "E407.left", {"start": v(-192.33, 115.51) * mm, "end": v(-192.33, 102.15) * mm});
            skLineSegment(sketch, "E407.right", {"start": v(-184.02, 115.51) * mm, "end": v(-184.02, 102.15) * mm});
            skLineSegment(sketch, "E408.bottom", {"start": v(-190.86, 60.11) * mm, "end": v(-185.16, 60.11) * mm});
            skLineSegment(sketch, "E408.top", {"start": v(-190.86, 47.57) * mm, "end": v(-185.16, 47.57) * mm});
            skLineSegment(sketch, "E408.left", {"start": v(-190.86, 60.11) * mm, "end": v(-190.86, 47.57) * mm});
            skLineSegment(sketch, "E408.right", {"start": v(-185.16, 60.11) * mm, "end": v(-185.16, 47.57) * mm});
            skLineSegment(sketch, "E409", {"start": v(-227.85, 107.45) * mm, "end": v(-227.85, 92.46) * mm});
            skLineSegment(sketch, "E410", {"start": v(-227.85, 92.46) * mm, "end": v(-232.9, 91.32) * mm});
            skLineSegment(sketch, "E411", {"start": v(-232.9, 91.32) * mm, "end": v(-232.9, 105.9) * mm});
            skLineSegment(sketch, "E412", {"start": v(-232.9, 105.9) * mm, "end": v(-227.85, 107.45) * mm});
            skLineSegment(sketch, "E413", {"start": v(-228.75, 137.76) * mm, "end": v(-228.75, 122.85) * mm});
            skLineSegment(sketch, "E414", {"start": v(-228.75, 122.85) * mm, "end": v(-232.17, 121.87) * mm});
            skLineSegment(sketch, "E415", {"start": v(-232.17, 121.87) * mm, "end": v(-232.17, 135.64) * mm});
            skLineSegment(sketch, "E416", {"start": v(-232.17, 135.64) * mm, "end": v(-228.75, 137.76) * mm});
            skLineSegment(sketch, "E417", {"start": v(-276.78, 50.14) * mm, "end": v(-284.24, 49.27) * mm});
            skLineSegment(sketch, "E418", {"start": v(-284.24, 49.27) * mm, "end": v(-284.34, 65.55) * mm});
            skLineSegment(sketch, "E419", {"start": v(-284.34, 65.55) * mm, "end": v(-277.27, 66.32) * mm});
            skLineSegment(sketch, "E420", {"start": v(-277.27, 66.32) * mm, "end": v(-276.78, 50.14) * mm});
            skLineSegment(sketch, "E421", {"start": v(-300.13, 48.88) * mm, "end": v(-305.56, 47.92) * mm});
            skLineSegment(sketch, "E422", {"start": v(-305.56, 47.92) * mm, "end": v(-305.56, 62.06) * mm});
            skLineSegment(sketch, "E423", {"start": v(-305.56, 62.06) * mm, "end": v(-300.43, 62.84) * mm});
            skLineSegment(sketch, "E424", {"start": v(-300.43, 62.84) * mm, "end": v(-300.13, 48.88) * mm});
            skLineSegment(sketch, "E425", {"start": v(-317.28, 47.14) * mm, "end": v(-322.3, 46.63) * mm});
            skLineSegment(sketch, "E426", {"start": v(-322.3, 46.63) * mm, "end": v(-322.3, 61.13) * mm});
            skLineSegment(sketch, "E427", {"start": v(-322.3, 61.13) * mm, "end": v(-317.34, 61.74) * mm});
            skLineSegment(sketch, "E428", {"start": v(-317.34, 61.74) * mm, "end": v(-317.28, 47.14) * mm});
            skLineSegment(sketch, "E429", {"start": v(-333.18, 59.13) * mm, "end": v(-333.18, 45.93) * mm});
            skLineSegment(sketch, "E430", {"start": v(-333.18, 45.93) * mm, "end": v(-337.46, 45.48) * mm});
            skLineSegment(sketch, "E431", {"start": v(-337.46, 45.48) * mm, "end": v(-337.46, 58.44) * mm});
            skLineSegment(sketch, "E432", {"start": v(-337.46, 58.44) * mm, "end": v(-333.18, 59.13) * mm});
            skLineSegment(sketch, "E433", {"start": v(-317.28, 11.51) * mm, "end": v(-272.28, 4.34) * mm});
            skLineSegment(sketch, "E434", {"start": v(-272.28, 4.34) * mm, "end": v(-272.28, 5.8) * mm});
            skLineSegment(sketch, "E435", {"start": v(-272.28, 5.8) * mm, "end": v(-317.28, 12.98) * mm});
            skLineSegment(sketch, "E436", {"start": v(-317.28, 12.98) * mm, "end": v(-317.28, 11.51) * mm});
            skLineSegment(sketch, "E437", {"start": v(-214.6, 37.04) * mm, "end": v(-214.6, 19.5) * mm});
            skLineSegment(sketch, "E438", {"start": v(-214.6, 19.5) * mm, "end": v(-213.3, 19.5) * mm});
            skLineSegment(sketch, "E439", {"start": v(-213.3, 19.5) * mm, "end": v(-213.3, 37.04) * mm});
            skLineSegment(sketch, "E440", {"start": v(-213.3, 37.04) * mm, "end": v(-214.68, 37.1) * mm});
            skLineSegment(sketch, "E441.bottom", {"start": v(-450.85, 320.77) * mm, "end": v(25.4, 320.77) * mm});
            skLineSegment(sketch, "E441.top", {"start": v(-450.85, -25.4) * mm, "end": v(25.4, -25.4) * mm});
            skLineSegment(sketch, "E441.left", {"start": v(-450.85, 320.77) * mm, "end": v(-450.85, -25.4) * mm});
            skLineSegment(sketch, "E441.right", {"start": v(25.4, 320.77) * mm, "end": v(25.4, -25.4) * mm});
            skLineSegment(sketch, "E442", {"start": v(-11.37, 91.58) * mm, "end": v(0, 92.8) * mm});
            skLineSegment(sketch, "E443", {"start": v(-10.82, 88.84) * mm, "end": v(0, 88.84) * mm});
            skArc(sketch, "E444", {"start": v(-161.5, 16.07) * mm, "mid": v(-157.66, 18.78) * mm, "end": v(-155.68, 23.05) * mm});
            skArc(sketch, "E445", {"start": v(-167.7, 0) * mm, "mid": v(-164.54, 3.27) * mm, "end": v(-161.89, 6.96) * mm});
            skArc(sketch, "E446", {"start": v(-161.25, 15.26) * mm, "mid": v(-157.16, 18.24) * mm, "end": v(-154.93, 22.8) * mm});
            skArc(sketch, "E447", {"start": v(-166.42, 0) * mm, "mid": v(-163.51, 2.92) * mm, "end": v(-161.2, 6.33) * mm});
            skLineSegment(sketch, "E448", {"start": v(-161.2, 6.33) * mm, "end": v(-161.89, 6.96) * mm});
            skLineSegment(sketch, "E449", {"start": v(-154.93, 22.8) * mm, "end": v(-155.68, 23.05) * mm});
            skLineSegment(sketch, "E450", {"start": v(-161.25, 15.26) * mm, "end": v(-161.5, 16.07) * mm});
            skLineSegment(sketch, "E451", {"start": v(-151.52, 151.57) * mm, "end": v(-151.52, 166.96) * mm});
            skLineSegment(sketch, "E452", {"start": v(-151.52, 166.96) * mm, "end": v(-161.02, 171.61) * mm});
            skLineSegment(sketch, "E453", {"start": v(-161.02, 171.61) * mm, "end": v(-161.02, 184.84) * mm});
            skLineSegment(sketch, "E454", {"start": v(-161.02, 184.84) * mm, "end": v(-166.32, 187.92) * mm});
            skLineSegment(sketch, "E455", {"start": v(-166.32, 187.92) * mm, "end": v(-167.28, 172.37) * mm});
            skLineSegment(sketch, "E456", {"start": v(-167.28, 172.37) * mm, "end": v(-171.26, 173.15) * mm});
            skLineSegment(sketch, "E457", {"start": v(-171.26, 173.15) * mm, "end": v(-170.79, 189.68) * mm});
            skLineSegment(sketch, "E458", {"start": v(-170.79, 189.68) * mm, "end": v(-174.34, 191.74) * mm});
            skLineSegment(sketch, "E459.0", {"start": v(-171.82, 189.1) * mm, "end": v(-174.85, 190.86) * mm});
            skLineSegment(sketch, "E459.1", {"start": v(-172.3, 172.32) * mm, "end": v(-171.82, 189.1) * mm});
            skLineSegment(sketch, "E459.2", {"start": v(-166.34, 171.15) * mm, "end": v(-172.3, 172.32) * mm});
            skLineSegment(sketch, "E459.3", {"start": v(-165.4, 186.22) * mm, "end": v(-166.34, 171.15) * mm});
            skLineSegment(sketch, "E459.4", {"start": v(-152.54, 151.57) * mm, "end": v(-152.54, 166.33) * mm});
            skLineSegment(sketch, "E459.5", {"start": v(-152.54, 166.33) * mm, "end": v(-162.03, 170.98) * mm});
            skLineSegment(sketch, "E459.6", {"start": v(-162.03, 170.98) * mm, "end": v(-162.03, 184.26) * mm});
            skLineSegment(sketch, "E459.7", {"start": v(-162.03, 184.26) * mm, "end": v(-165.4, 186.22) * mm});
            skLineSegment(sketch, "E460", {"start": v(-151.52, 151.57) * mm, "end": v(-152.54, 151.57) * mm});
            skLineSegment(sketch, "E461", {"start": v(-174.85, 190.86) * mm, "end": v(-174.34, 191.74) * mm});
            skLineSegment(sketch, "E462", {"start": v(-110.78, 142.26) * mm, "end": v(-110.78, 152.92) * mm});
            skLineSegment(sketch, "E463", {"start": v(-110.78, 152.92) * mm, "end": v(-112.72, 153.3) * mm});
            skLineSegment(sketch, "E464", {"start": v(-112.72, 153.3) * mm, "end": v(-112.9, 143.91) * mm});
            skLineSegment(sketch, "E465", {"start": v(-112.9, 143.91) * mm, "end": v(-115.53, 145.66) * mm});
            skLineSegment(sketch, "E466", {"start": v(-115.53, 145.66) * mm, "end": v(-115.43, 153.5) * mm});
            skLineSegment(sketch, "E467", {"start": v(-115.43, 153.5) * mm, "end": v(-122.8, 157.19) * mm});
            skLineSegment(sketch, "E468", {"start": v(-122.8, 157.19) * mm, "end": v(-124.63, 156.22) * mm});
            skLineSegment(sketch, "E469", {"start": v(-124.63, 156.22) * mm, "end": v(-124.63, 155.18) * mm});
            skLineSegment(sketch, "E470", {"start": v(-124.63, 155.18) * mm, "end": v(-122.72, 156.27) * mm});
            skLineSegment(sketch, "E471", {"start": v(-122.72, 156.27) * mm, "end": v(-116.16, 153) * mm});
            skLineSegment(sketch, "E472", {"start": v(-116.16, 153) * mm, "end": v(-116.16, 145.15) * mm});
            skLineSegment(sketch, "E473", {"start": v(-116.16, 145.15) * mm, "end": v(-112.81, 142.8) * mm});
            skLineSegment(sketch, "E474", {"start": v(-110.78, 142.26) * mm, "end": v(-111.26, 142.53) * mm});
            skLineSegment(sketch, "E475", {"start": v(-111.26, 142.53) * mm, "end": v(-111.29, 152.27) * mm});
            skLineSegment(sketch, "E476", {"start": v(-111.29, 152.27) * mm, "end": v(-112.12, 152.39) * mm});
            skLineSegment(sketch, "E477", {"start": v(-112.12, 152.39) * mm, "end": v(-112.44, 142.42) * mm});
            skLineSegment(sketch, "E478", {"start": v(-112.44, 142.42) * mm, "end": v(-112.81, 142.8) * mm});
            skLineSegment(sketch, "E479", {"start": v(-450.85, 0) * mm, "end": v(25.4, 0) * mm});
            skSolve(sketch);
        }
        {
            var Q0;
            Q0=makeQuery(id+"F0.imprint","IMPRINT",FACE,{"disambiguationData":[TD([[makeQuery(id+"F0.imprint","IMPRINT",EDGE,{"derivedFrom":sQuery(id+"F0.wireOp",EDGE,"E0")}),-1.0]])]});
            extrude(context, id + "F1", {"entities" : qUnion([Q0]), "depth" : 25.4 * mm, "offsetDistance" : 25.4 * mm});
        }
    });
